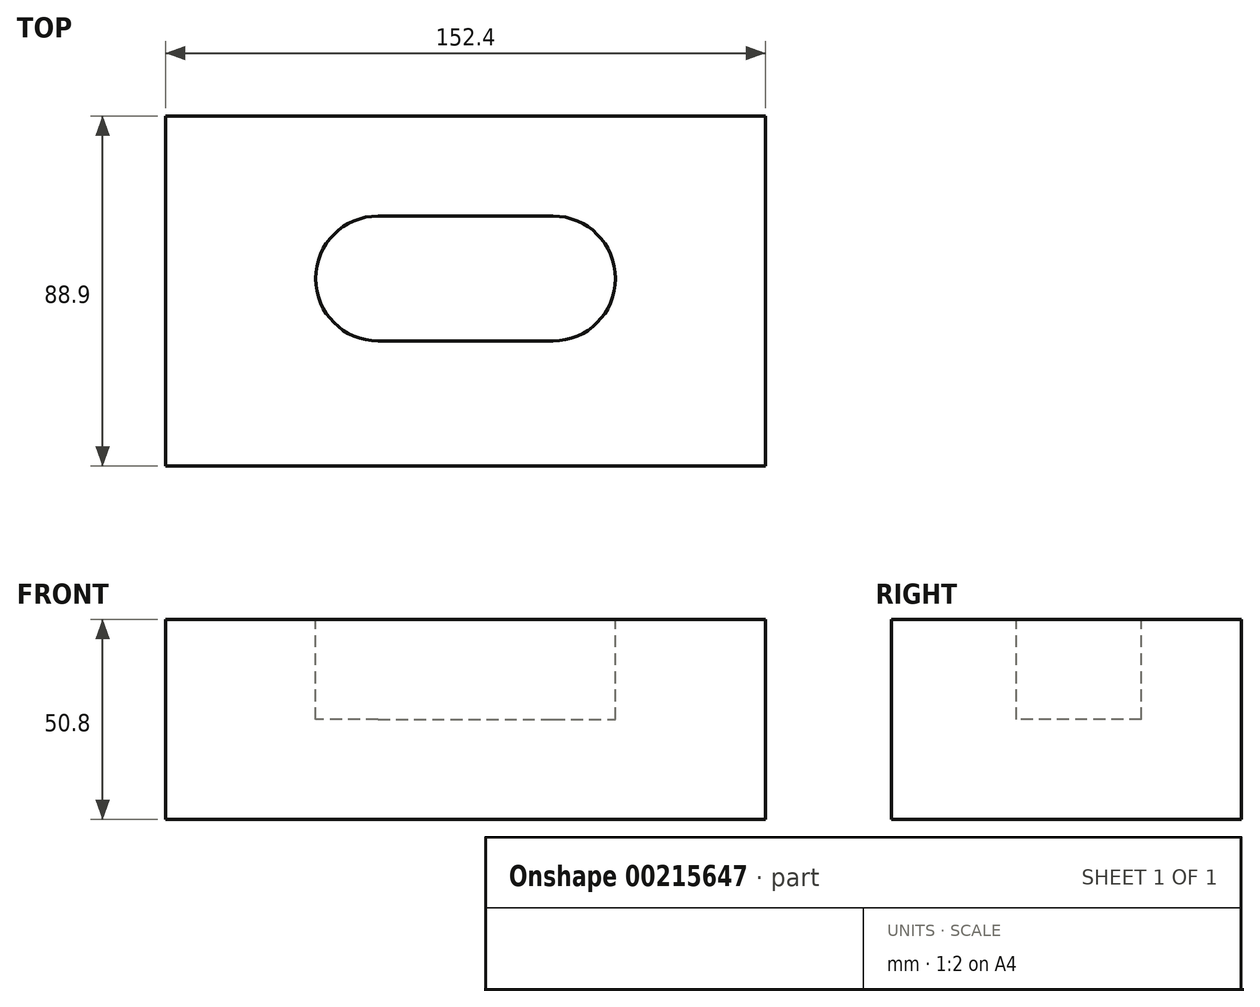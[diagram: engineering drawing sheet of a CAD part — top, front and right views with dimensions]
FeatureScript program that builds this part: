
annotation { "Feature Type Name" : "Feature", "Feature Type Description" : "" }
export const myFeature = defineFeature(function(context is Context, id is Id, definition is map)
    precondition{}
    {
        {
            var Q0;
            Q0=qCreatedBy(makeId("Top.planeOp"),FACE);
            var sketch = newSketch(context, id + "F0", { "sketchPlane" : qUnion([Q0])});
            skLineSegment(sketch, "E0.bottom", {"start": v(0, 0) * mm, "end": v(152.4, 0) * mm});
            skLineSegment(sketch, "E0.top", {"start": v(0, 88.9) * mm, "end": v(152.4, 88.9) * mm});
            skLineSegment(sketch, "E0.left", {"start": v(0, 0) * mm, "end": v(0, 88.9) * mm});
            skLineSegment(sketch, "E0.right", {"start": v(152.4, 0) * mm, "end": v(152.4, 88.9) * mm});
            skSolve(sketch);
        }
        {
            var Q0;
            Q0 = qSketchRegion(id + "F0", true);
            extrude(context, id + "F1", {"entities" : qUnion([Q0]), "depth" : 50.8 * mm});
        }
        {
            var Q0;
            Q0=makeQuery(id+"F1.opExtrude","CAP_FACE",FACE,{"disambiguationData":[OSD([sQuery(id+"F0.wireOp",EDGE,"E0.bottom"),sQuery(id+"F0.wireOp",EDGE,"E0.top"),sQuery(id+"F0.wireOp",EDGE,"E0.left"),sQuery(id+"F0.wireOp",EDGE,"E0.right")])],"isStart":false});
            var sketch = newSketch(context, id + "F2", { "sketchPlane" : qUnion([Q0])});
            skLineSegment(sketch, "E1", {"start": v(53.98, 31.75) * mm, "end": v(98.43, 31.75) * mm});
            skArc(sketch, "E2", {"start": v(98.43, 31.75) * mm, "mid": v(114.3, 47.62) * mm, "end": v(98.43, 63.5) * mm});
            skArc(sketch, "E3", {"start": v(53.98, 31.75) * mm, "mid": v(38.1, 47.62) * mm, "end": v(53.98, 63.5) * mm});
            skLineSegment(sketch, "E4", {"start": v(53.98, 63.5) * mm, "end": v(98.43, 63.5) * mm});
            skSolve(sketch);
        }
        {
            var Q0;
            Q0 = qSketchRegion(id + "F2", true);
            extrude(context, id + "F3", {"entities" : qUnion([Q0]), "operationType" : NewBodyOperationType.REMOVE, "oppositeDirection" : true, "depth" : 25.4 * mm});
        }
    });
